# Revit family: LEO_D_L
name_source: partatom
category: Mechanical Equipment
revit_build: Autodesk Revit LT 2018 (Build: 20180329_1100(x64)
units: mm (PartAtom-declared; Revit-internal decimal feet)

## family parameters
Cut with Voids When Loaded = No
Host = Face
Part Type = Normal
Room Calculation Point = No
Round Connector Dimension = Use Diameter
Shared = No

## types (9) — shared parameters
Description = Destratifikátor
Distance from the ceiling = 1000 mm  [stored 3.28084 ft]
Fan = axial, single-phase, AC with 3-speed motor
IP = 54
Load classification = Silnik
Manufacturer = Hydronic Systems Prague s.r.o.
Mass of unit = 13.90 kg
Material = EPP-grey
Max. current consumption = 1 A
Power factor = 1
Supply voltage = 230 V
Type Comments = vnitřní instalace, podstropní, vertikální; max. teplota okolí +50°C; IP54; Qmax=5200 m3/h při 3. rychlosti
URL = www.hydronic.cz
zero-valued in all types: Default Elevation

## per-type parameters (varying)
| type | Airflow | Apparent power | Assembly Code | Model | Standard equipment |
| LEO DT L, 1 rychlost | 2800.0 m³/h | 138 VA | 52076; LEO DT L (vč. integrovaného pokojového termostatu)  - 1 rychlost | LEO DT L | pokojový termostat umístěný na opláštění jednotky |
| LEO DT L, 2 rychlost | 4200.0 m³/h | 230 VA | 52076; LEO DT L (vč. integrovaného pokojového termostatu)  - 2 rychlost | LEO DT L | pokojový termostat umístěný na opláštění jednotky |
| LEO DT L, 3 rychlost | 5200.0 m³/h | 299 VA | 52076; LEO DT L (vč. integrovaného pokojového termostatu)  - 3 rychlost | LEO DT L | pokojový termostat umístěný na opláštění jednotky |
| LEO D L BMS, 1 rychlost | 2800.0 m³/h | 138 VA | 52081; LEO D L BMS (vč. DRV-D + 1xPT1000)  - 1 rychlost | LEO D L BMS | DRV + PT-1000 |
| LEO D L BMS, 2 rychlost | 4200.0 m³/h | 230 VA | 52081; LEO D L BMS (vč. DRV-D + 1xPT1000)  - 2 rychlost | LEO D L BMS | DRV + PT-1000 |
| LEO D L BMS, 3 rychlost | 5200.0 m³/h | 299 VA | 52081; LEO D L BMS (vč. DRV-D + 1xPT1000)  - 3 rychlost | LEO D L BMS | DRV + PT-1000 |
| LEO D L, 1 rychlost | 2800.0 m³/h | 138 VA | 52071; LEO D L - 1 rychlost | LEO D L |  |
| LEO D L, 2 rychlost | 4200.0 m³/h | 230 VA | 52071; LEO D L - 2 rychlost | LEO D L |  |
| LEO D L, 3 rychlost | 5200.0 m³/h | 299 VA | 52071; LEO D L - 3 rychlost | LEO D L |  |

note: [stored X ft] marks values corroborated as IEEE doubles in the binary element streams (Revit-internal decimal feet)
